# Revit family: O12901001_Lavamanos Cascade Vessel Blanco
name_source: partatom
category: Plumbing Fixtures
units: mm (PartAtom-declared; Revit-internal decimal feet)

## family parameters
Always vertical = Yes
Cut with Voids When Loaded = No
OmniClass Number = 23.31.13.11
OmniClass Title = Single Sinks
Part Type = Normal
Room Calculation Point = No
Round Connector Dimension = Use Diameter
Shared = No
Work Plane-Based = No

## types (1)
- O12901001_Lavamanos Cascade Vessel Blanco
    Acabado = Brillante
    Alto = 16 cm
    Ancho = 46 cm
    Colección = Cascade
    Creado por = IDD
    Description = La línea Cascade nace a partir de la propuesta de CORONA de entregar un diseño amigable y sorprendente, que busca facilitar la tareas y funciones del espacio del baño a nuestros consumidores, su diseño se inspira en la caída del agua, por lo tanto, su forma es fluida, pero con una mezcla de robustez que hace de la línea CASCADE un producto funcional, pero a la vez resistente brindando mayor comodidad en su uso los lavamanos vessel de esta linea se caracterizan por sus Pozos amplios de 46cm y profundidad de 14cm que permite mayor comodidad al realizar diferentes actividades cotidianas, además de minimizar el salpique al momento del uso Tecnología AQUAFLOW: Superficie homogénea que impide la acumulación de agua y residuos. Tecnología COVERGLOSS: alta resistencia al rayado y a cambios de temperatura. Diseño guiado por la forma y la función.Acabado uniforme.
    Dimensión del pozo = 46
    Diámetro del desagüe = 43.5 mm
    Fecha de creación = 30/07/2020
    Forma = Ovalado
    Garantía = Garantía completa para siempre en la porcelana
    Largo = 39.5 cm
    Línea = Cascade
    Material = Corona_Porcelana_Sanitaria
    Materiales = Porcelana sanitaria
    No incluye = Grifería
    Productos compatibles = Grifería monocontrol alta
    Profundidad del pozo = 14 cm
    Resistencia = Alta resistencia al rayado y cambios de temperatura
    Tecnologías = CoverGloss Aquaflow
    Tipo de desagüe = Expuesto
    Tipo de instalación = A pared
    Tipo de lavamanos = Vessel
    URL = https://corona.co
    Uso = Residencial

## geometry (parser evidence)
native form markers: Sweep x5
no freeform markers — native parametric forms only
